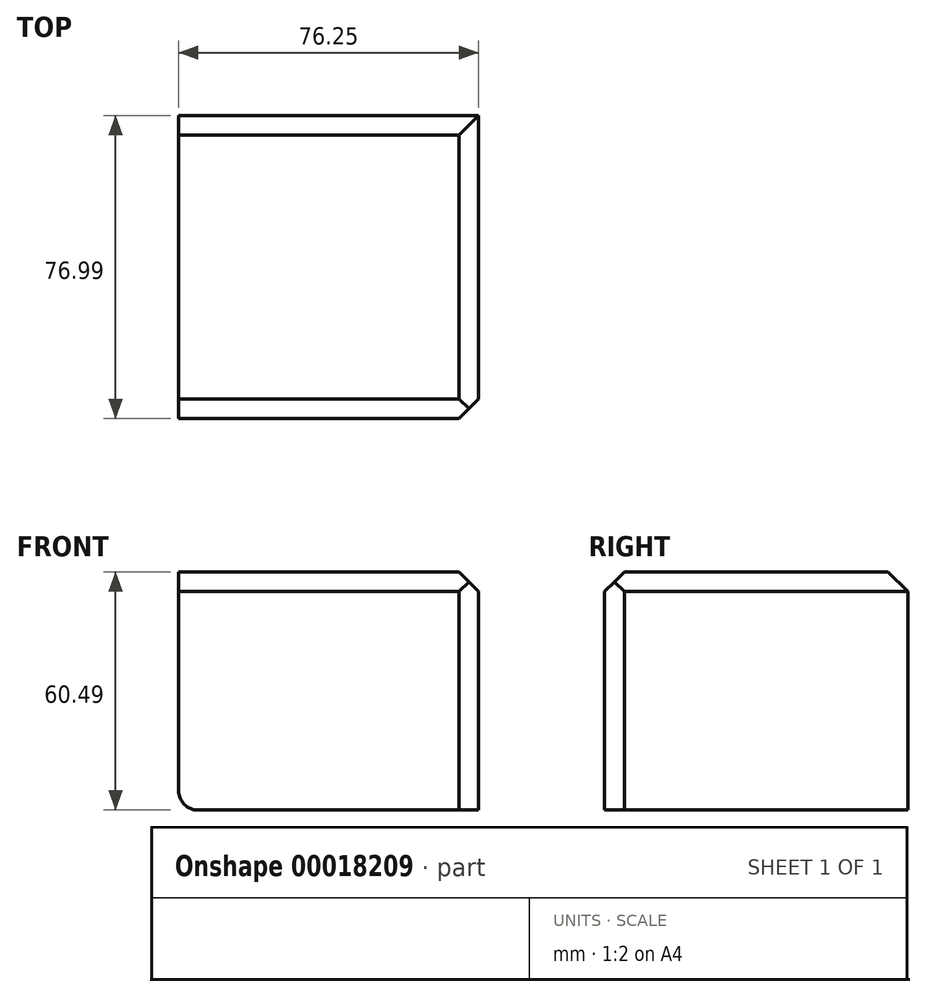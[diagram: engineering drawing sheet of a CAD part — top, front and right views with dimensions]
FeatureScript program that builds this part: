
annotation { "Feature Type Name" : "Feature", "Feature Type Description" : "" }
export const myFeature = defineFeature(function(context is Context, id is Id, definition is map)
    precondition{}
    {
        {
            var Q0;
            Q0=qCreatedBy(makeId("Top.planeOp"),FACE);
            var sketch = newSketch(context, id + "F0", { "sketchPlane" : qUnion([Q0])});
            skLineSegment(sketch, "E0.bottom", {"start": v(0, 0) * mm, "end": v(76.25, 0) * mm});
            skLineSegment(sketch, "E0.top", {"start": v(0, -77) * mm, "end": v(76.25, -77) * mm});
            skLineSegment(sketch, "E0.left", {"start": v(0, 0) * mm, "end": v(0, -77) * mm});
            skLineSegment(sketch, "E0.right", {"start": v(76.25, 0) * mm, "end": v(76.25, -77) * mm});
            skSolve(sketch);
        }
        {
            var Q0;
            Q0=makeQuery(id+"F0.imprint","IMPRINT",FACE,{"disambiguationData":[TD([[makeQuery(id+"F0.imprint","IMPRINT",EDGE,{"derivedFrom":sQuery(id+"F0.wireOp",EDGE,"E0.bottom")}),-1.0]])]});
            extrude(context, id + "F1", {"entities" : qUnion([Q0]), "depth" : 60.5 * mm});
        }
        {
            var Q0;
            Q0=makeQuery(id+"F1.opExtrude","CAP_EDGE",EDGE,{"disambiguationData":[OSD([sQuery(id+"F0.wireOp",EDGE,"E0.right")])],"isStart":false});
            var Q1;
            Q1=makeQuery(id+"F1.opExtrude","SWEPT_EDGE",EDGE,{"disambiguationData":[OSD([sQuery(id+"F0.wireOp",EDGE,"E0.top"),sQuery(id+"F0.wireOp",EDGE,"E0.right")])]});
            chamfer(context, id + "F2", {"entities" : qUnion([Q0, Q1]), "width" : 5 * mm, "tangentPropagation" : true});
        }
        {
            var Q0;
            Q0=makeQuery(id+"F1.opExtrude","CAP_EDGE",EDGE,{"disambiguationData":[OSD([sQuery(id+"F0.wireOp",EDGE,"E0.top")])],"isStart":false});
            var Q1;
            Q1=makeQuery(id+"F1.opExtrude","CAP_EDGE",EDGE,{"disambiguationData":[OSD([sQuery(id+"F0.wireOp",EDGE,"E0.bottom")])],"isStart":false});
            chamfer(context, id + "F3", {"entities" : qUnion([Q0, Q1]), "width" : 5 * mm, "tangentPropagation" : true});
        }
        {
            var Q0;
            Q0=makeQuery(id+"F1.opExtrude","CAP_EDGE",EDGE,{"disambiguationData":[OSD([sQuery(id+"F0.wireOp",EDGE,"E0.left")])],"isStart":true});
            fillet(context, id + "F4", {"entities" : qUnion([Q0]), "radius" : 5 * mm, "tangentPropagation" : true, "allowEdgeOverflow" : false});
        }
    });
